# Revit family: CFP-ECM 4T
name_source: partatom
category: Attrezzatura meccanica
revit_build: Autodesk Revit 2017 (Build: 20160225_1515(x64)
units: mm (PartAtom-declared; Revit-internal decimal feet)

## family parameters
Basato su piano di lavoro = Sì
Condiviso = No
Punto di calcolo locali = No
Quota connettore circolare = Usa diametro
Sempre verticale = Sì
Taglio con vuoti quando caricato = Sì
Tipo di parte = Normale

## types (14) — shared parameters
Lwaste = 14 mm  [stored 0.0459318 ft]
Modello = CFP-ECM Frontal Connections
Produttore = Sabiana s.r.l.
Prospetto di default = 1219.2 mm  [stored 4 ft]
body = metallo
dist L fermo = 12.75 mm
dist T fermo = 6.25 mm  [stored 0.0205052 ft]
fermi = plastic
grill = griglia
waste H = 10 mm  [stored 0.0328084 ft]

## per-type parameters (varying)
| type | size |
| CFP-ECM 1200-175-350 | 1200175 |
| CFP-ECM 900-130-330 | 900130 |
| CFP-ECM 1200-130-330 | 1200130 |
| CFP-ECM 1000-175-350 | 1000175 |
| CFP-ECM 1400-130-330 | 1400130 |
| CFP-ECM 1400-175-350 | 1400175 |
| CFP-ECM 1700-130-330 | 1700130 |
| CFP-ECM 1700-175-350 | 1700175 |
| CFP-ECM 2000-130-330 | 2000130 |
| CFP-ECM 2000-175-350 | 2000175 |
| CFP-ECM 2500-130-330 | 2500130 |
| CFP-ECM 2500-175-350 | 2500175 |
| CFP-ECM 3000-130-330 | 3000130 |
| CFP-ECM 3000-175-350 | 3000175 |

note: [stored X ft] marks values corroborated as IEEE doubles in the binary element streams (Revit-internal decimal feet)
